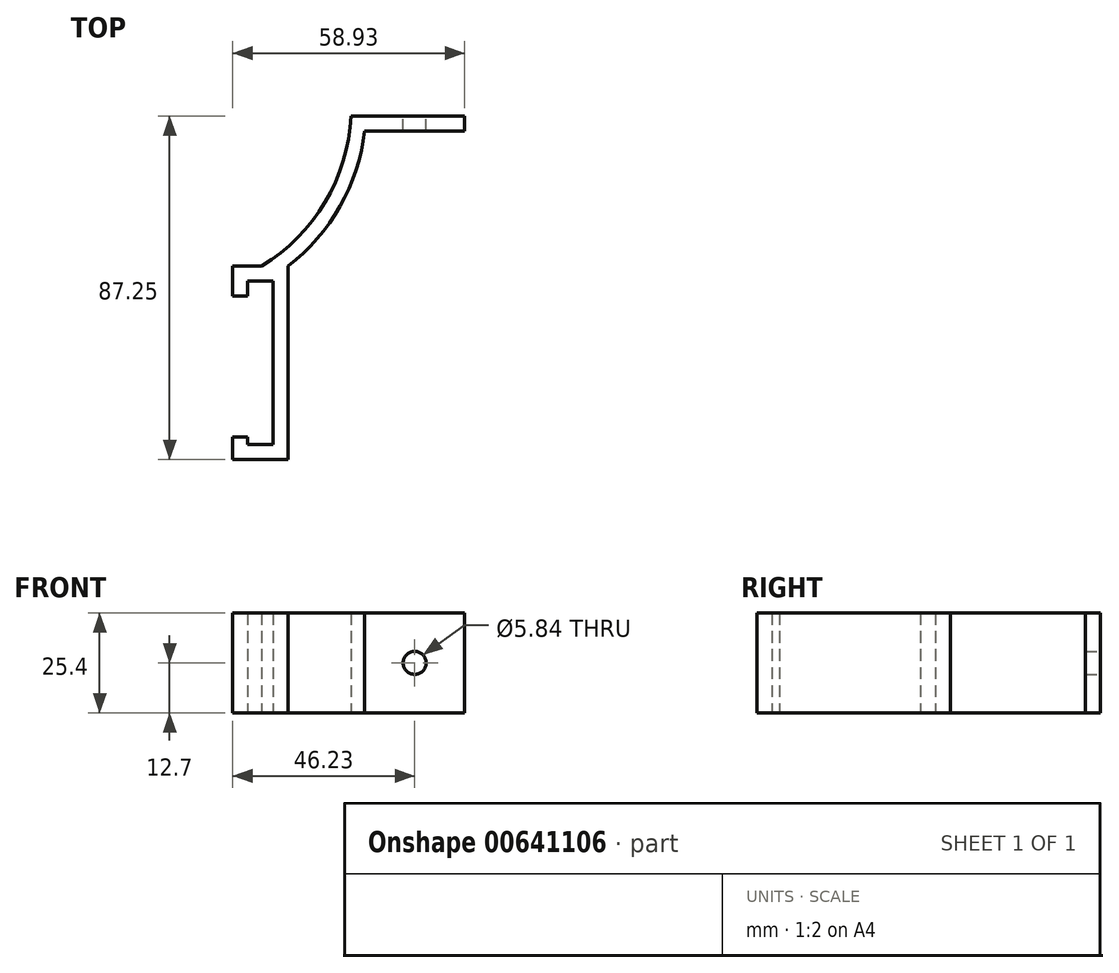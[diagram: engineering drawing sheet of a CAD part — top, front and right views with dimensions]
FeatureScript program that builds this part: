
annotation { "Feature Type Name" : "Feature", "Feature Type Description" : "" }
export const myFeature = defineFeature(function(context is Context, id is Id, definition is map)
    precondition{}
    {
        {
            var Q0;
            Q0=qCreatedBy(makeId("Top.planeOp"),FACE);
            var sketch = newSketch(context, id + "F0", { "sketchPlane" : qUnion([Q0])});
            skLineSegment(sketch, "E0", {"start": v(-18.35, 20.13) * mm, "end": v(-18.35, -21.4) * mm});
            skLineSegment(sketch, "E1", {"start": v(-18.35, -21.4) * mm, "end": v(-24.83, -21.4) * mm});
            skLineSegment(sketch, "E2", {"start": v(-24.83, -19.5) * mm, "end": v(-28.64, -19.5) * mm});
            skLineSegment(sketch, "E3", {"start": v(-14.54, -25.2) * mm, "end": v(-14.54, 20.13) * mm});
            skLineSegment(sketch, "E4", {"start": v(-28.64, 23.94) * mm, "end": v(-28.64, 16.32) * mm});
            skLineSegment(sketch, "E5", {"start": v(-28.64, 16.32) * mm, "end": v(-24.83, 16.32) * mm});
            skLineSegment(sketch, "E6", {"start": v(-24.83, 16.32) * mm, "end": v(-24.83, 20.13) * mm});
            skLineSegment(sketch, "E7", {"start": v(-24.83, 20.13) * mm, "end": v(-18.35, 20.13) * mm});
            skLineSegment(sketch, "E8", {"start": v(30.29, 62.04) * mm, "end": v(1.38, 62.04) * mm});
            skLineSegment(sketch, "E9", {"start": v(30.29, 62.04) * mm, "end": v(30.29, 58.23) * mm});
            skLineSegment(sketch, "E10", {"start": v(30.29, 58.23) * mm, "end": v(4.89, 58.23) * mm});
            skPoint(sketch, "E11.orphan", {"position": v(1.08, 58.23) * mm});
            skLineSegment(sketch, "E12", {"start": v(-14.54, 20.13) * mm, "end": v(-14.54, 23.94) * mm});
            skPoint(sketch, "E13.end.orphan", {"position": v(30.29, 23.94) * mm});
            skArc(sketch, "E14", {"start": v(-14.54, 23.94) * mm, "mid": v(-1.37, 39.12) * mm, "end": v(4.89, 58.23) * mm});
            skLineSegment(sketch, "E15", {"start": v(-14.54, -25.2) * mm, "end": v(-28.64, -25.2) * mm});
            skArc(sketch, "E16.0", {"start": v(-21.28, 23.94) * mm, "mid": v(-5.17, 40.15) * mm, "end": v(1.38, 62.04) * mm});
            skLineSegment(sketch, "E17", {"start": v(-28.64, 23.94) * mm, "end": v(-21.28, 23.94) * mm});
            skPoint(sketch, "E18.orphan", {"position": v(1.08, 62.04) * mm});
            skLineSegment(sketch, "E19", {"start": v(-28.64, -19.5) * mm, "end": v(-28.64, -25.2) * mm});
            skLineSegment(sketch, "E20", {"start": v(-24.83, -19.5) * mm, "end": v(-24.83, -21.4) * mm});
            skSolve(sketch);
        }
        {
            var Q0;
            Q0=makeQuery(id+"F0.imprint","IMPRINT",FACE,{"disambiguationData":[TD([[makeQuery(id+"F0.imprint","IMPRINT",EDGE,{"derivedFrom":sQuery(id+"F0.wireOp",EDGE,"E0")}),1.0]])]});
            extrude(context, id + "F1", {"entities" : qUnion([Q0]), "depth" : 25.4 * mm, "offsetDistance" : 25.4 * mm});
        }
        {
            var Q0;
            Q0=makeQuery(id+"F1.opExtrude","SWEPT_FACE",FACE,{"disambiguationData":[OSD([sQuery(id+"F0.wireOp",EDGE,"E8")])]});
            var sketch = newSketch(context, id + "F2", { "sketchPlane" : qUnion([Q0])});
            skCircle(sketch, "E21", {"center": v(-17.59, 12.7) * mm, "radius": 2.92 * mm});
            skPoint(sketch, "E21.centerSnap0", {"position": v(-30.29, 12.7) * mm});
            skSolve(sketch);
        }
        {
            var Q0;
            Q0=makeQuery(id+"F2.imprint","IMPRINT",FACE,{"disambiguationData":[TD([[makeQuery(id+"F2.imprint","IMPRINT",EDGE,{"derivedFrom":sQuery(id+"F2.wireOp",EDGE,"E21")}),1.0]])]});
            extrude(context, id + "F3", {"entities" : qUnion([Q0]), "operationType" : NewBodyOperationType.REMOVE, "endBound" : BoundingType.THROUGH_ALL, "oppositeDirection" : true, "depth" : 25.4 * mm, "offsetDistance" : 25.4 * mm});
        }
    });
